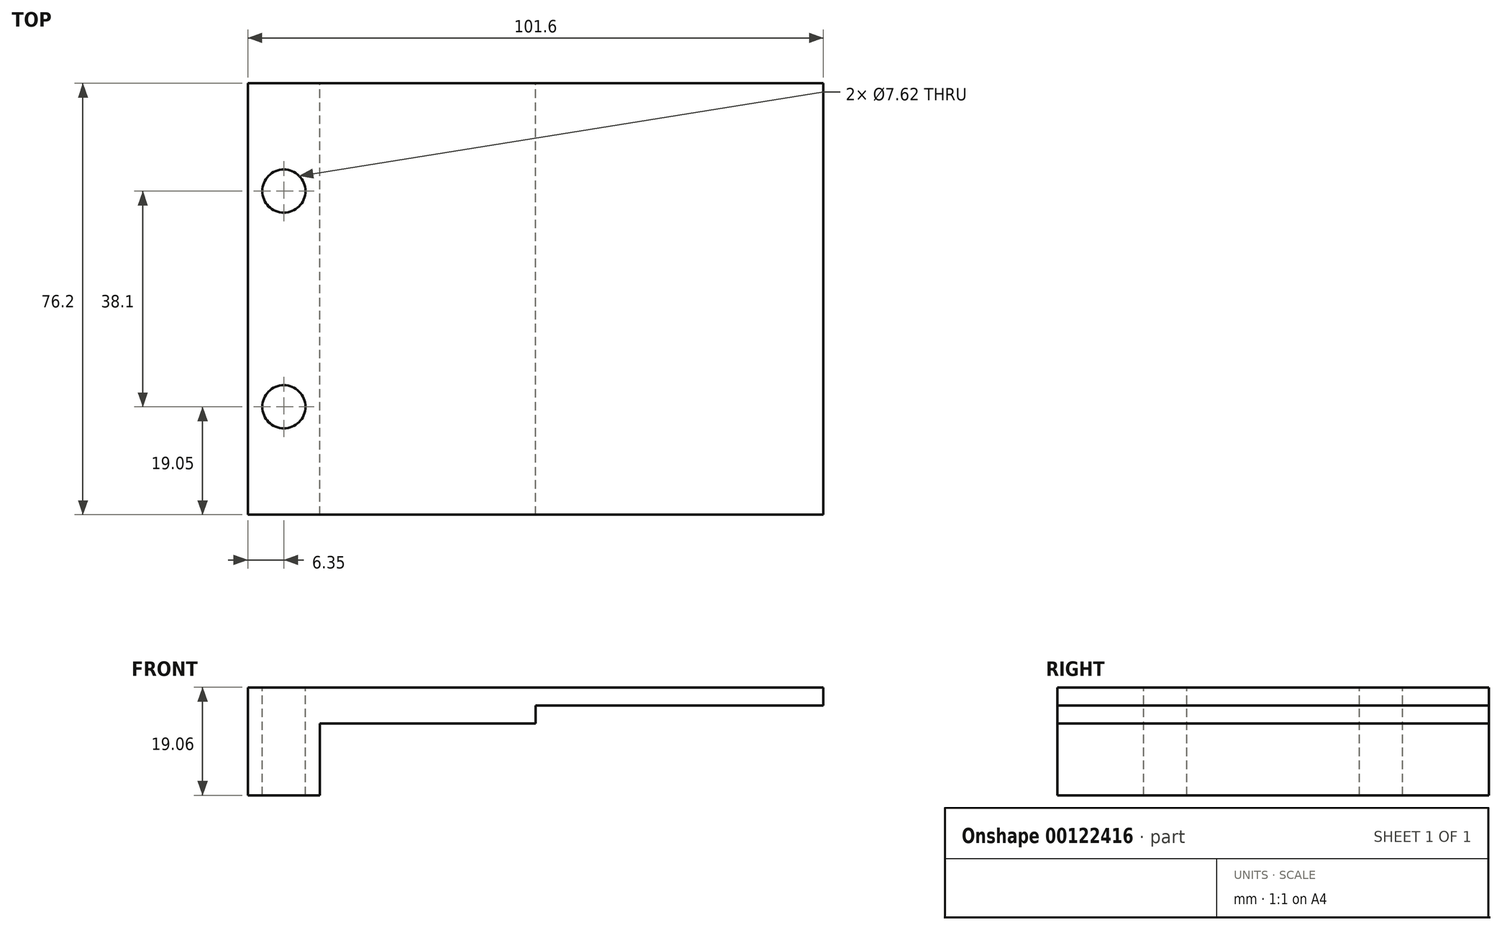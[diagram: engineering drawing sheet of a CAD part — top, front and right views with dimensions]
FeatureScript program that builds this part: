
annotation { "Feature Type Name" : "Feature", "Feature Type Description" : "" }
export const myFeature = defineFeature(function(context is Context, id is Id, definition is map)
    precondition{}
    {
        {
            var Q0;
            Q0=qCreatedBy(makeId("Front.planeOp"),FACE);
            var sketch = newSketch(context, id + "F0", { "sketchPlane" : qUnion([Q0])});
            skLineSegment(sketch, "E0.bottom", {"start": v(-25.4, 3.17) * mm, "end": v(25.4, 3.17) * mm});
            skLineSegment(sketch, "E0.top", {"start": v(-25.4, -3.18) * mm, "end": v(25.4, -3.18) * mm});
            skLineSegment(sketch, "E0.left", {"start": v(-25.4, 3.17) * mm, "end": v(-25.4, -3.17) * mm});
            skLineSegment(sketch, "E0.right", {"start": v(25.4, 3.17) * mm, "end": v(25.4, -3.17) * mm});
            skPoint(sketch, "E0.middle", {"position": v(0, 0) * mm});
            skLineSegment(sketch, "E1.bottom", {"start": v(25.4, 3.17) * mm, "end": v(76.2, 3.17) * mm});
            skLineSegment(sketch, "E1.top", {"start": v(25.4, 0) * mm, "end": v(76.2, 0) * mm});
            skLineSegment(sketch, "E1.left", {"start": v(25.4, 3.17) * mm, "end": v(25.4, 0) * mm});
            skLineSegment(sketch, "E1.right", {"start": v(76.2, 3.18) * mm, "end": v(76.2, 0) * mm});
            skSolve(sketch);
        }
        {
            var Q0;
            {var subQ0=sQuery(id+"F0.wireOp",EDGE,"E1.bottom");var subQ2=sQuery(id+"F0.wireOp",EDGE,"E0.bottom");Q0=qUnion([makeQuery(id+"F0.imprint","IMPRINT",FACE,{"disambiguationData":[TD([[makeQuery(id+"F0.imprint","IMPRINT",EDGE,{"derivedFrom":subQ2}),-1.0]])]}),makeQuery(id+"F0.imprint","IMPRINT",FACE,{"disambiguationData":[TD([[makeQuery(id+"F0.imprint","IMPRINT",EDGE,{"derivedFrom":subQ0}),-1.0]])]})]);}
            extrude(context, id + "F1", {"entities" : qUnion([Q0]), "depth" : 76.2 * mm});
        }
        {
            var Q0;
            Q0=makeQuery(id+"F1.opExtrude","SWEPT_FACE",FACE,{"disambiguationData":[OSD([sQuery(id+"F0.wireOp",EDGE,"E0.bottom"),sQuery(id+"F0.wireOp",EDGE,"E1.bottom")])]});
            var sketch = newSketch(context, id + "F2", { "sketchPlane" : qUnion([Q0])});
            skPoint(sketch, "E2.endSnap0", {"position": v(-25.4, -38.1) * mm});
            skLineSegment(sketch, "E3.bottom", {"start": v(-12.77, -19.05) * mm, "end": v(-25.33, -19.05) * mm});
            skLineSegment(sketch, "E3.top", {"start": v(-12.77, -57.15) * mm, "end": v(-25.33, -57.15) * mm});
            skLineSegment(sketch, "E3.left", {"start": v(-12.77, -19.05) * mm, "end": v(-12.77, -57.15) * mm});
            skLineSegment(sketch, "E3.right", {"start": v(-25.33, -19.05) * mm, "end": v(-25.33, -57.15) * mm});
            skPoint(sketch, "E3.middle", {"position": v(-19.05, -38.1) * mm});
            skCircle(sketch, "E4", {"center": v(-19.05, -19.05) * mm, "radius": 3.81 * mm});
            skCircle(sketch, "E5", {"center": v(-19.05, -57.15) * mm, "radius": 3.81 * mm});
            skSolve(sketch);
        }
        {
            var Q0;
            {var subQ0=sQuery(id+"F2.wireOp",EDGE,"E4");var subQ1=sQuery(id+"F2.wireOp",EDGE,"E3.bottom");var subQ2=makeQuery(id+"F2.imprint","INTERSECT",VERTEX,{"disambiguationData":[OD(0.0)],"derivedFrom":[subQ1,subQ0]});Q0=makeQuery(id+"F2.imprint","IMPRINT",FACE,{"disambiguationData":[TD([[makeQuery(id+"F2.imprint","IMPRINT",EDGE,{"disambiguationData":[TD([[subQ2,-1.0]])],"derivedFrom":subQ1}),-1.0]])]});}
            var Q1;
            {var subQ0=sQuery(id+"F2.wireOp",EDGE,"E4");var subQ1=sQuery(id+"F2.wireOp",EDGE,"E3.bottom");var subQ2=makeQuery(id+"F2.imprint","INTERSECT",VERTEX,{"disambiguationData":[OD(0.0)],"derivedFrom":[subQ1,subQ0]});Q1=makeQuery(id+"F2.imprint","IMPRINT",FACE,{"disambiguationData":[TD([[makeQuery(id+"F2.imprint","IMPRINT",EDGE,{"disambiguationData":[TD([[subQ2,-1.0]])],"derivedFrom":subQ1}),1.0]])]});}
            var Q2;
            {var subQ0=sQuery(id+"F2.wireOp",EDGE,"E5");var subQ1=sQuery(id+"F2.wireOp",EDGE,"E3.top");var subQ2=makeQuery(id+"F2.imprint","INTERSECT",VERTEX,{"disambiguationData":[OD(0.0)],"derivedFrom":[subQ1,subQ0]});Q2=makeQuery(id+"F2.imprint","IMPRINT",FACE,{"disambiguationData":[TD([[makeQuery(id+"F2.imprint","IMPRINT",EDGE,{"disambiguationData":[TD([[subQ2,-1.0]])],"derivedFrom":subQ1}),-1.0]])]});}
            var Q3;
            {var subQ0=sQuery(id+"F2.wireOp",EDGE,"E5");var subQ1=sQuery(id+"F2.wireOp",EDGE,"E3.top");var subQ2=makeQuery(id+"F2.imprint","INTERSECT",VERTEX,{"disambiguationData":[OD(0.0)],"derivedFrom":[subQ1,subQ0]});Q3=makeQuery(id+"F2.imprint","IMPRINT",FACE,{"disambiguationData":[TD([[makeQuery(id+"F2.imprint","IMPRINT",EDGE,{"disambiguationData":[TD([[subQ2,-1.0]])],"derivedFrom":subQ1}),1.0]])]});}
            extrude(context, id + "F3", {"entities" : qUnion([Q0, Q1, Q2, Q3]), "operationType" : NewBodyOperationType.REMOVE, "endBound" : BoundingType.THROUGH_ALL, "oppositeDirection" : true, "depth" : 25.4 * mm});
        }
        {
            var Q0;
            Q0=makeQuery(id+"F1.opExtrude","SWEPT_FACE",FACE,{"disambiguationData":[OSD([sQuery(id+"F0.wireOp",EDGE,"E0.top")])]});
            var sketch = newSketch(context, id + "F4", { "sketchPlane" : qUnion([Q0])});
            skLineSegment(sketch, "E6.bottom", {"start": v(-25.4, 76.2) * mm, "end": v(-12.7, 76.2) * mm});
            skLineSegment(sketch, "E6.top", {"start": v(-25.4, 0) * mm, "end": v(-12.7, 0) * mm});
            skLineSegment(sketch, "E6.left", {"start": v(-25.4, 76.2) * mm, "end": v(-25.4, 0) * mm});
            skLineSegment(sketch, "E6.right", {"start": v(-12.7, 76.2) * mm, "end": v(-12.7, 0) * mm});
            skCircle(sketch, "E7", {"center": v(-19.05, 57.15) * mm, "radius": 3.81 * mm});
            skCircle(sketch, "E8", {"center": v(-19.05, 19.05) * mm, "radius": 3.81 * mm});
            skSolve(sketch);
        }
        {
            var Q0;
            Q0 = qSketchRegion(id + "F4", true);
            extrude(context, id + "F5", {"entities" : qUnion([Q0]), "operationType" : NewBodyOperationType.ADD, "depth" : 12.7 * mm});
        }
    });
